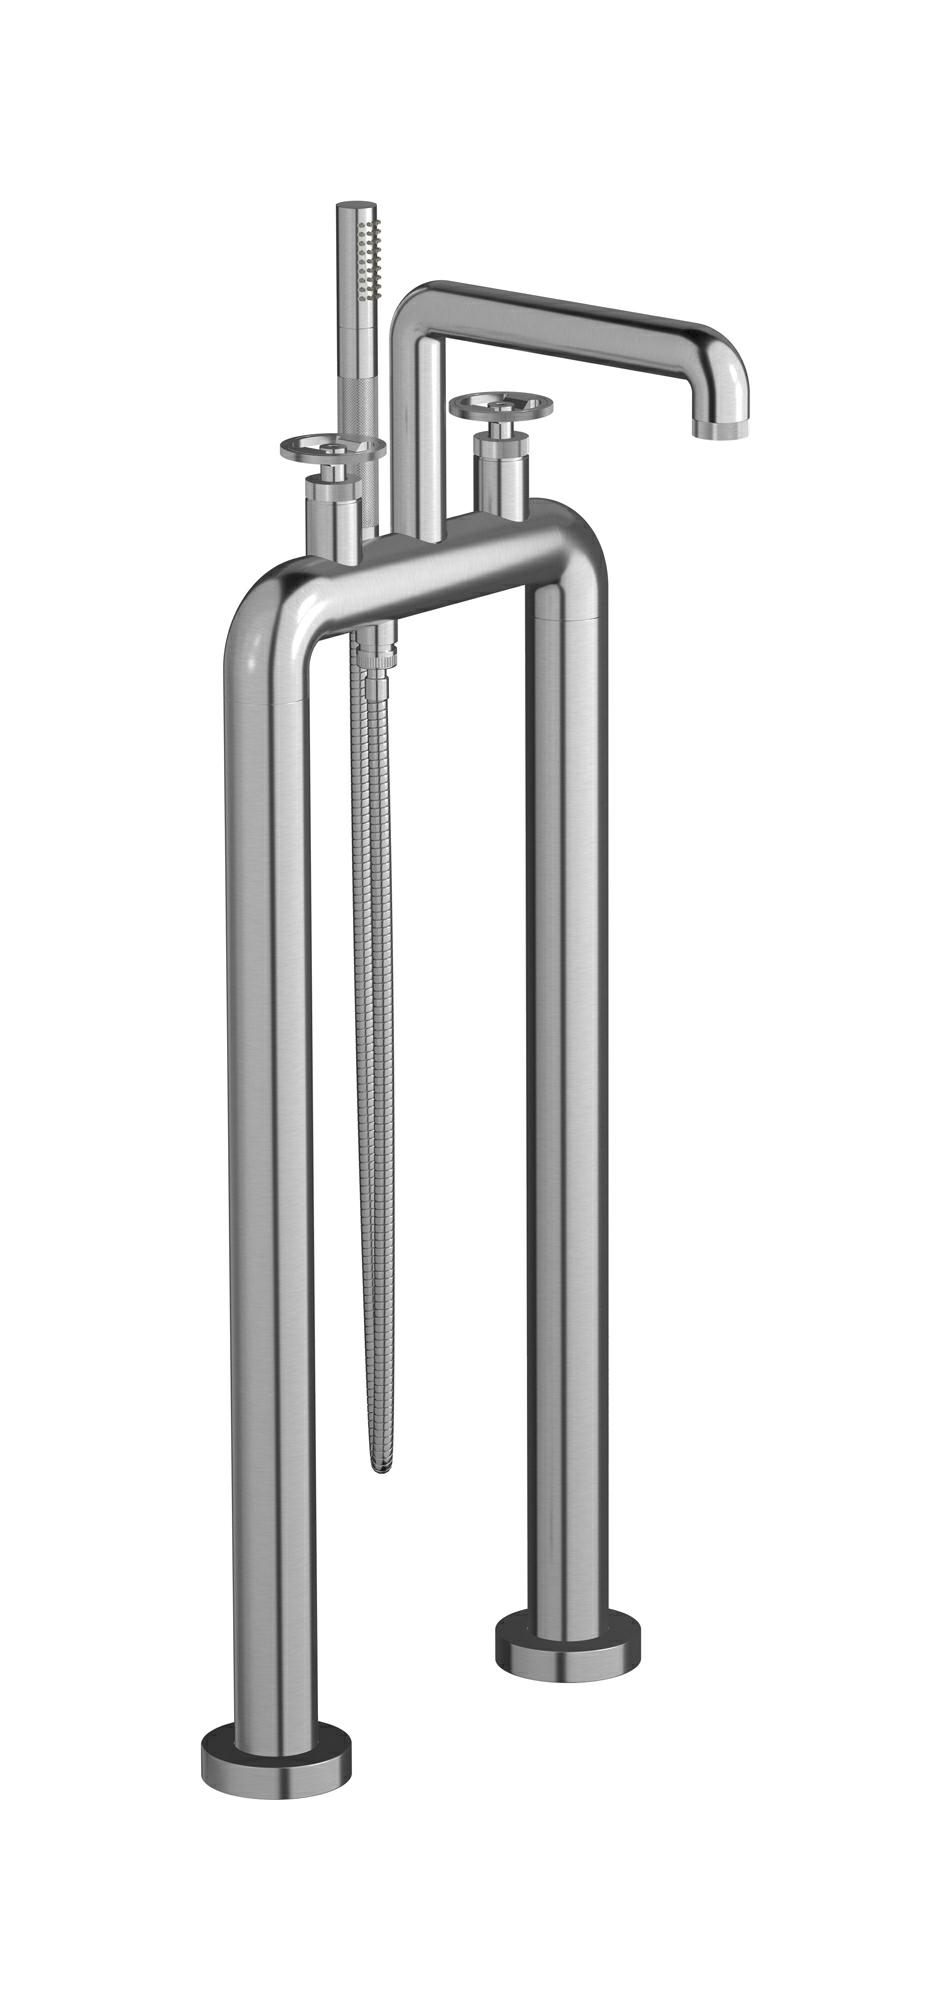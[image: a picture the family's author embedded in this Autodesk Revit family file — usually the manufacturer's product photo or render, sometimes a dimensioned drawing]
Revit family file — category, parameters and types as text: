
# Revit family: B1700
name_source: partatom
category: Apparecchi idraulici
units: mm (PartAtom-declared; Revit-internal decimal feet)

## family parameters
Basato su piano di lavoro = No
Condiviso = No
Mantieni orientamento annotazione = No
Numero OmniClass = 23.45.55.17
Punto di calcolo locali = No
Quota connettore circolare = Usa diametro
Sempre verticale = Sì
Taglio con vuoti quando caricato = No
Tipo di parte = Normale
Titolo OmniClass = Mixing Faucets

## types (13) — shared parameters
Cold water inlet = 10 mm  [stored 0.0328084 ft]
Commenti sul tipo = Freestanding two columns bath filler with shower kit
Connessione CW = No
Connessione HW = No
Connessione di scarico = No
Connessione di ventilazione = No
Descrizione = Freestanding two columns bath filler with shower kit
Hot water inlet = 10 mm  [stored 0.0328084 ft]
Produttore = IB Rubinetterie S.p.A.
URL = https://www.weareib.it
zero-valued in all types: Prospetto di default

## per-type parameters (varying)
| type | Finishes surface | Immagine tipo | Modello |
| Chrome | IB_Chrome | B1700CC.jpg | B1700CC |
| Black Chrome | IB_Black chrome | B1700CF.jpg | B1700CF |
| Brushed Black Chrome | IB_Brushed black chrome | B1700CS.jpg | B1700CS |
| Pale Gold | IB_Pale gold | B1700II.jpg | B1700II |
| Brushed Pale Gold | IB_brushed pale gold | B1700IS.jpg | B1700IS |
| Matt Black | IB_matt black | B1700NP.jpg | B1700NP |
| Natural Brass | IB_Brass | B1700ON.jpg | B1700ON |
| Gold | IB_gold | B1700OO.jpg | B1700OO |
| Brushed Gold | IB_brushed gold | B1700OS.jpg | B1700OS |
| Rose Gold | IB_Rose gold | B1700RS.jpg | B1700RS |
| Brushed Rose Gold | IB_Brushed rose gold | B1700SR.jpg | B1700SR |
| Brushed Nickel | IB_Brushed nickel | B1700SS.jpg | B1700SS |
| Modern Bronze | IB_Modern bronze | B1700MB.jpg | B1700MB |

note: [stored X ft] marks values corroborated as IEEE doubles in the binary element streams (Revit-internal decimal feet)
